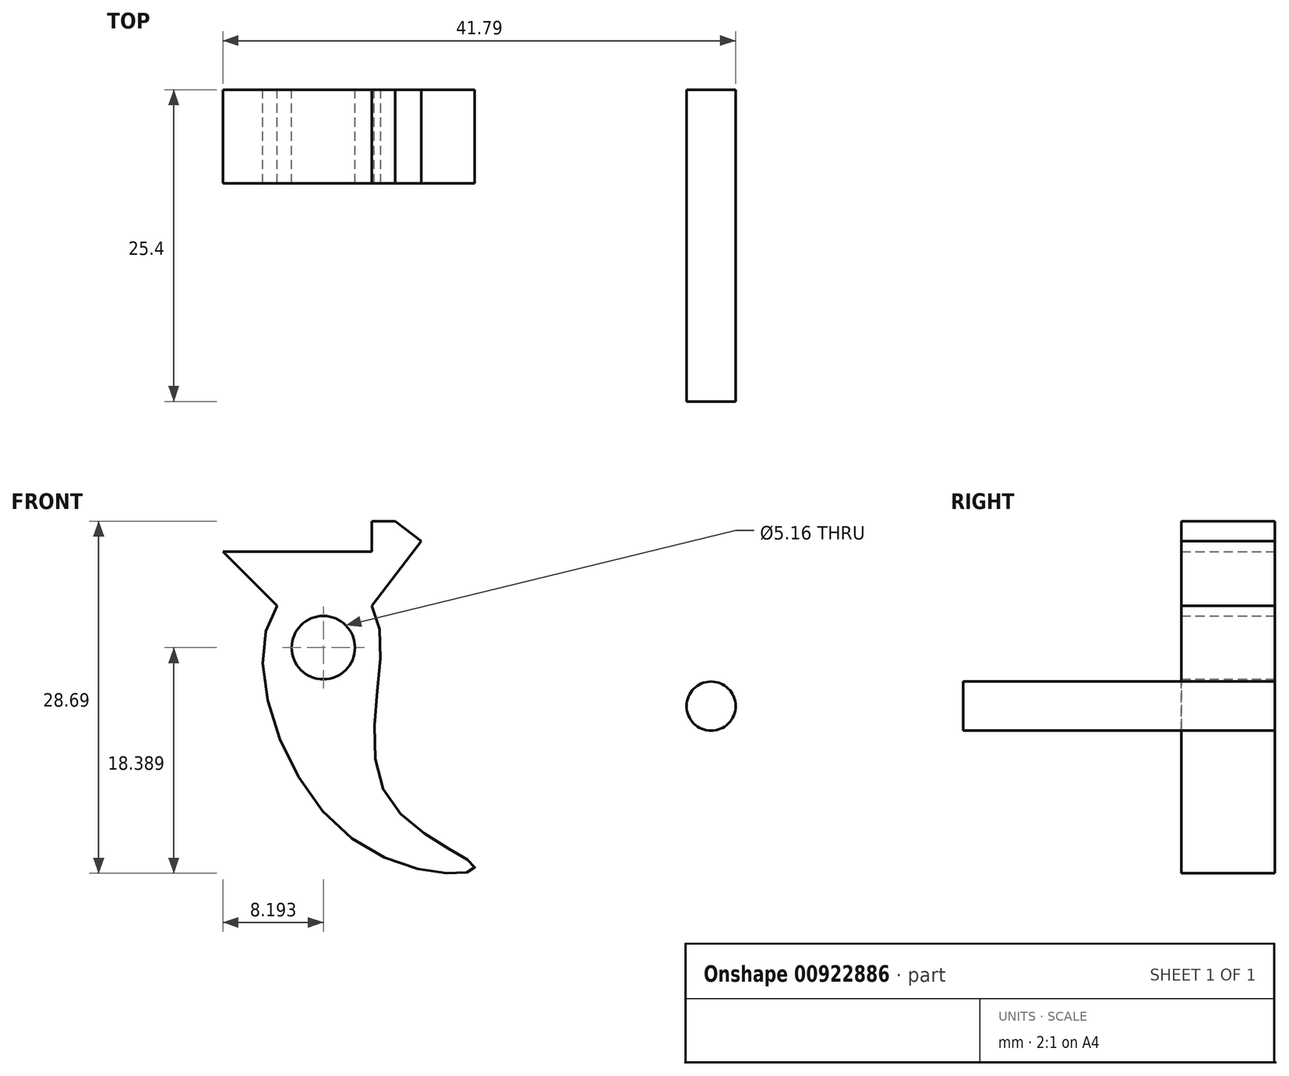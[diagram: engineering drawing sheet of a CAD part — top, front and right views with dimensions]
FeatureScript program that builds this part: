
annotation { "Feature Type Name" : "Feature", "Feature Type Description" : "" }
export const myFeature = defineFeature(function(context is Context, id is Id, definition is map)
    precondition{}
    {
        {
            var Q0;
            Q0=qCreatedBy(makeId("Front.planeOp"),FACE);
            var sketch = newSketch(context, id + "F0", { "sketchPlane" : qUnion([Q0])});
            skFitSpline(sketch, "E0", {"points": [v(-34.04, 38.14) * mm, v(-27.96, 19.17) * mm, v(-17.95, 16.85) * mm, v(-25.28, 22.93) * mm, v(-26.35, 38.14) * mm, v(-34.04, 38.14) * mm]});
            skCircle(sketch, "E1", {"center": v(-30.29, 34.74) * mm, "radius": 2.58 * mm});
            skCircle(sketch, "E2", {"center": v(1.31, 29.97) * mm, "radius": 2 * mm});
            skLineSegment(sketch, "E3", {"start": v(-26.35, 38.14) * mm, "end": v(-22.31, 43.41) * mm});
            skLineSegment(sketch, "E4", {"start": v(-22.31, 43.41) * mm, "end": v(-24.44, 45.04) * mm});
            skLineSegment(sketch, "E5", {"start": v(-24.44, 45.04) * mm, "end": v(-26.35, 42.55) * mm});
            skLineSegment(sketch, "E6", {"start": v(-26.35, 42.55) * mm, "end": v(-38.48, 42.55) * mm});
            skLineSegment(sketch, "E7", {"start": v(-38.48, 42.55) * mm, "end": v(-34.04, 38.14) * mm});
            skLineSegment(sketch, "E8", {"start": v(-26.35, 42.55) * mm, "end": v(-26.35, 45.04) * mm});
            skLineSegment(sketch, "E9", {"start": v(-24.44, 45.04) * mm, "end": v(-26.35, 45.04) * mm});
            skSolve(sketch);
        }
        {
            var Q0;
            Q0 = qSketchRegion(id + "F0", true);
            extrude(context, id + "F1", {"entities" : qUnion([Q0]), "depth" : 7.62 * mm, "offsetDistance" : 25.4 * mm});
        }
        {
            var Q0;
            Q0=makeQuery(id+"F1.opExtrude","CAP_FACE",FACE,{"disambiguationData":[OSD([sQuery(id+"F0.wireOp",EDGE,"E2")])],"isStart":false});
            extrude(context, id + "F2", {"entities" : qUnion([Q0]), "operationType" : NewBodyOperationType.ADD, "depth" : 17.78 * mm, "offsetDistance" : 25.4 * mm});
        }
    });
